# Revit family: R-CVA-0007
name_source: partatom
category: Fenêtres
units: mm (PartAtom-declared; Revit-internal decimal feet)

## family parameters
Couper avec des vides une fois chargée = Non
Hôte = Mur
Partagée = Non
Point de calcul de pièce = Non
Toujours verticalement = Oui

## types (1)
- CVA-0007
    Acoustique = Rw (C ; Ctr) = 39 (-1 ; -3) dB
    Ambrasure = 0 mm  [stored 0 ft]
    Applique = Non
    Certification = PEFC
    Châssis Hauteur Hors Tout = 2095 mm  [stored 6.87336 ft]
    Châssis Largeur Hors Tout = 481 mm  [stored 1.57808 ft]
    Construction analytique = <Aucun>
    Description = Chassis vitré, EI30, 39(-1; -3) dB (performance du vitrage), résistance aux chocs 2B2, sans résistance aux UV, avec parcloses bois, sur cadre bois
    Fabricant = Montibert
    Fiche_Produit = CVA-0007
    Huisserie_Delardage Largeur = 8 mm  [stored 0.0262467 ft]
    Huisserie_Délardage Bas Epaisseur = 8 mm  [stored 0.0262467 ft]
    Huisserie_Délardage Haut  Epaisseur = 8 mm  [stored 0.0262467 ft]
    Huisserie_Délardage_Bas = Non
    Huisserie_Délardage_Haut = Non
    Huisserie_Feuillure Epaisseur = 41 mm  [stored 0.134514 ft]
    Huisserie_Feuillure Largeur = 24 mm  [stored 0.0787402 ft]
    Huisserie_Feuillure_Basse = Oui
    Huisserie_Feuillure_Haute = Non
    Huisserie_Feuillure_Sans = Non
    Huisserie_Matériau = BER
    Huisserie_Profil_Epaisseur = 78 mm  [stored 0.255906 ft]
    Huisserie_Profil_Largeur = 50 mm  [stored 0.164042 ft]
    Huisserie_Rainure à Brique = Oui
    Huisserie_Rainure à Brique_Largeur = 8 mm  [stored 0.0262467 ft]
    Jeu Bas = 0 mm  [stored 0 ft]
    Jeu Haut = 0 mm  [stored 0 ft]
    Jeu Latéral 1 = 0 mm  [stored 0 ft]
    Jeu Latéral 2 = 0 mm  [stored 0 ft]
    Materiaux_Dominant = Bois
    Montant_1 = Non
    Montant_2 = Non
    Montant_Largeur = 72 mm  [stored 0.23622 ft]
    Note d'identification = CHASSIS VITRE EI30
    Parclosage à Recouvrement = Non
    Parclose Jeu Epaisseur = 1 mm  [stored 0.00328084 ft]
    Parclose Jeu Largeur = 0 mm  [stored 0 ft]
    Parclose Largeur = 24 mm  [stored 0.0787402 ft]
    Parclose Recouvrement Epaisseur = 6 mm  [stored 0.019685 ft]
    Parclose Recouvrement Largeur = 6 mm  [stored 0.019685 ft]
    Parcloses_Matériau = BER
    Profil 1_Largeur = 50 mm  [stored 0.164042 ft]
    Profil 1_Latéral = Non
    Profil 2_Largeur = 50 mm  [stored 0.164042 ft]
    Profil 2_Latéral = Non
    Profil Bas = Non
    Profil Bas_Largeur = 70 mm  [stored 0.229659 ft]
    Profil Haut = Non
    Profil Haut_Largeur = 50 mm  [stored 0.164042 ft]
    Profil_Délardage_Bas_Epaisseur = 8 mm  [stored 0.0262467 ft]
    Profil_Délardage_Haut_Epaisseur = 8 mm  [stored 0.0262467 ft]
    Profil_Délardage_Largeur = 8 mm  [stored 0.0262467 ft]
    Profil_Déplacement Vers Nu Ext = Oui
    Profil_Déplacement Vers Nu Int = Non
    Profil_Déplacement Vers l'Huisserie = Non
    Profil_Déplacement Vers le Mur = Oui
    Profil_Matériau = BER
    Profil_Rainure à Brique_ coté Ext = Oui
    Profil_Rainure à Brique_ coté Int = Oui
    Profils_Délardage Bas_coté Ext = Non
    Profils_Délardage Bas_coté Int = Non
    Profils_Délardage Haut_coté Ext = Non
    Profils_Délardage Haut_coté Int = Non
    Profils_Déplacement X = 8 mm  [stored 0.0262467 ft]
    Profils_Déplacement X' = 0 mm  [stored 0 ft]
    Profils_Déplacement Y = 0 mm  [stored 0 ft]
    Profils_Déplacement Y' = 8 mm  [stored 0.0262467 ft]
    Recouvrement = Oui
    Reference_Commerciale = C EI30 VAc
    Resistance_Chocs = 2B2 (900J)
    Resistance_Feu = E30-EW30
    Resistance_Humidite = Optionnel
    Sens_Feu = Recto / Verso
    Tunnel = Non
    URL = https://www.malerba.fr
    Vitrage Epaisseur = 17 mm
    Vitrage_Matériau = Verre
    X1'_Tunnel = 2095 mm  [stored 6.87336 ft]
    X1_Tunnel = 481 mm  [stored 1.57808 ft]
    X2'_Recouvrement et Applique = 2079 mm  [stored 6.82087 ft]
    X2_Recouvrement et Applique = 465 mm  [stored 1.52559 ft]
    X3'_Déduction Délardages Profils = 0 mm  [stored 0 ft]
    X3_Déduction Délardages Profils = 0 mm  [stored 0 ft]
    X4'_Déduction Délardages Huisseries = 16 mm  [stored 0.0524934 ft]
    X4_Déduction Délardages Huisseries = 16 mm  [stored 0.0524934 ft]
    X_Ambrasure = 0 mm  [stored 0 ft]
    X_Ambrasure Décalage Epaisseur = 0 mm  [stored 0 ft]
    X_Huisserie Décalage Hauteur = 0 mm  [stored 0 ft]
    X_Huisserie Décalage Hauteur_INV = 0 mm  [stored 0 ft]
    X_Huisserie Décalage Largeur = 0 mm  [stored 0 ft]
    X_Huisserie Décalage Largeur_INV = 0 mm  [stored 0 ft]
    X_Huisserie_Delardage Largeur = 8 mm  [stored 0.0262467 ft]
    X_Ouvertur Mur Largeur = 465 mm  [stored 1.52559 ft]
    X_Ouverture Mur Hauteur = 2079 mm  [stored 6.82087 ft]
    X_Profil 1_Largeur = 0 mm  [stored 0 ft]
    X_Profil 2_Largeur = 0 mm  [stored 0 ft]
    X_Profil Bas_Largeur = 0 mm  [stored 0 ft]
    X_Profil Haut_Largeur = 0 mm  [stored 0 ft]
    X_Profil_Délardage_Largeur = 8 mm  [stored 0.0262467 ft]

note: [stored X ft] marks values corroborated as IEEE doubles in the binary element streams (Revit-internal decimal feet)

## geometry (parser evidence)
native form markers: Blend x12
no freeform markers — native parametric forms only
